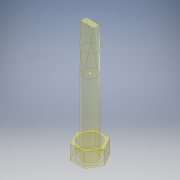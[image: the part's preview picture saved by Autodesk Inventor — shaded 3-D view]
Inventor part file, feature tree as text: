
AUTODESK INVENTOR PART (.ipt)
format: ipt  version: 2017 (Build 210142000, 142)  size: 180,224 bytes
history: native  units: mm
features: sketch x9, extrude x2, plane x2, loft x2, other x2
ambient origin geometry x8: Origin, YZ Plane, XZ Plane, XY Plane, X Axis, Y Axis, Z Axis, Center Point
bodies: Solid1 (feature_tree)
feature tree (17):
  extrude  "Extrusion1"  Depth=5.0mm TaperAngle=0.0deg
  extrude  "Extrusion2"  Depth=5.0mm TaperAngle=0.0deg
  plane  "Work Plane1"
  sketch  "Sketch5"  dims[d8=7.5mm d30=0.0mm d31=90.0deg]
  sketch  "Sketch6"  dims[d32=0.0mm d33=90.0deg d34=0.0mm d35=90.0deg]
  loft  "Loft3"
  plane  "Work Plane3"
  loft  "Loft4"
  sketch  "Sketch1"  dims[d2=7.0mm d3=5.0mm d4=0.0mm]
  sketch  "Sketch4"  dims[d5=5.0mm d6=25.0mm d7=0.0mm]
  sketch  "3D Sketch12"
  sketch  "3D Sketch13"
  sketch  "3D Sketch14"
  sketch  "3D Sketch15"
  other  "Edges3"
  sketch  "Sketch8"  dims[d36=0.0mm d37=90.0deg d38=0.0mm d39=90.0deg d40=0.0mm d41=90.0deg d42=7.5mm d44=0.0mm d45=90.0deg d46=0.0mm d47=90.0deg]
  other  "Edges4"
